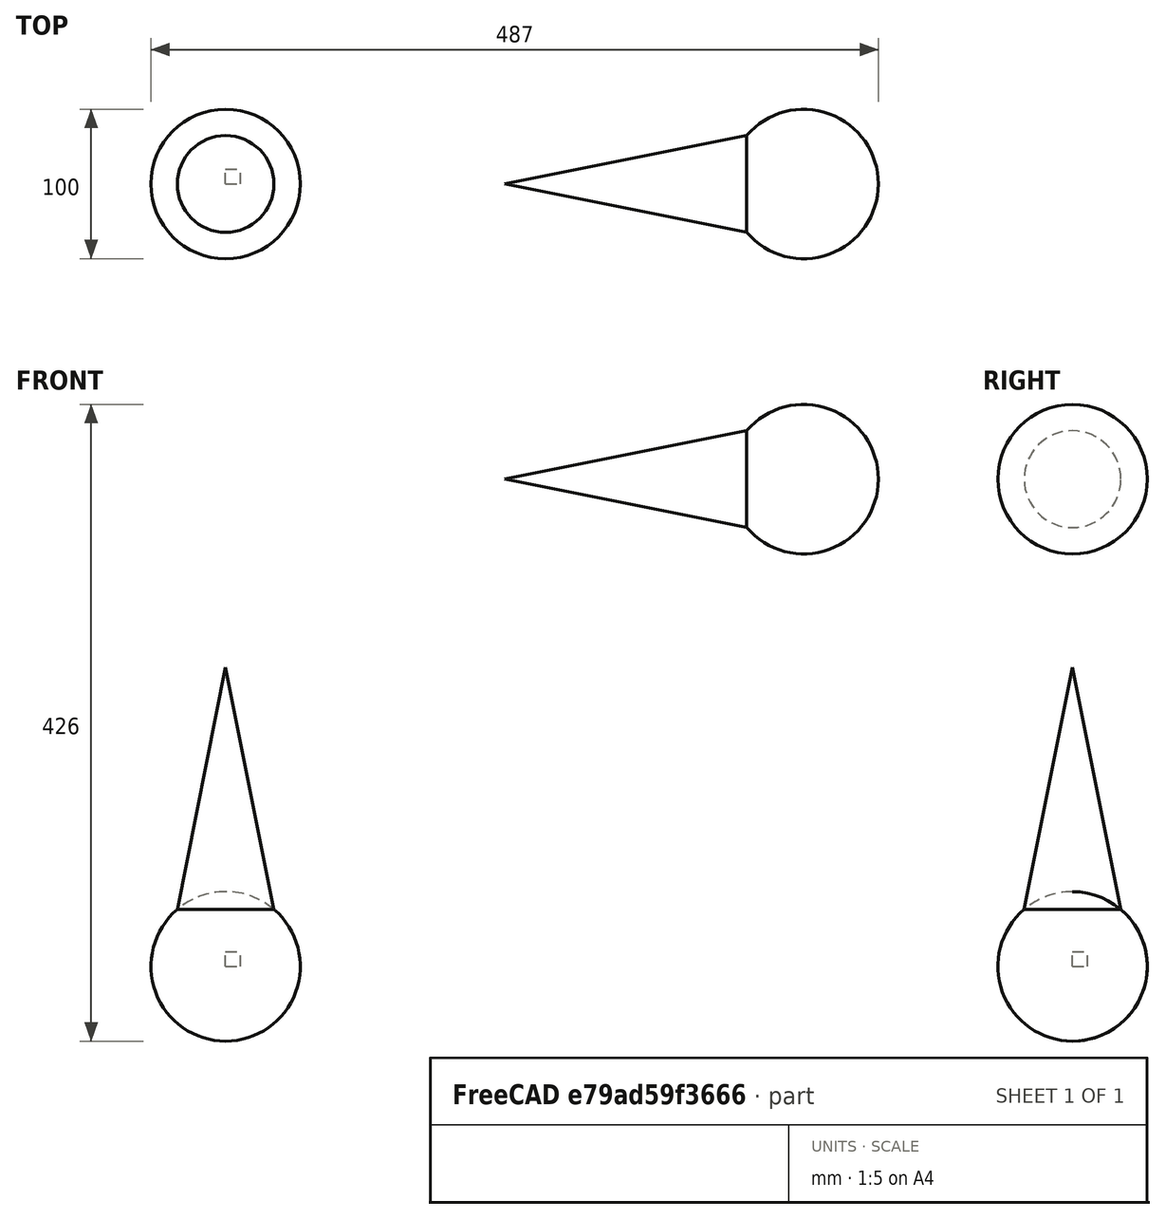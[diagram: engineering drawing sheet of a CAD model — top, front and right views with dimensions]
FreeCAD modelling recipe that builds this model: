
FCSTD DOCUMENT  (FreeCAD 0.22R36526 (Git))
Label: Bungee
License: All rights reserved
LicenseURL: http://en.wikipedia.org/wiki/All_rights_reserved
objects: App::DocumentObjectGroupPython×59, PartDesign::CoordinateSystem×7, App::Part×3, App::TextDocument×3, Part::Line×3, App::FeaturePython×3, Part::Sphere×2, Part::FeaturePython×2, App::MaterialObjectPython×2, Part::Cone×1, Part::MultiFuse×1, Part::Box×1
note: 17 computed .brp shape members not serialized (recipe doc carries the construction recipe); baked Part::Feature solids carry a one-line shape summary decoded from their .brp

FEATURE [Part::Sphere] Sphere
  Angle1 = -90
  Angle2 = 90
  Angle3 = 360
  AttacherType = Attacher::AttachEngine3D
  Radius = 50
FEATURE [Part::Sphere] Sphere001
  Angle1 = -90
  Angle2 = 90
  Angle3 = 360
  AttacherType = Attacher::AttachEngine3D
  Radius = 50
FEATURE [App::Part] Part  label="Fixed body"
  Group = -> [Sphere]
  Origin = -> Origin
FEATURE [Part::Cone] Cone
  Angle = 360
  AttacherType = Attacher::AttachEngine3D
  Height = 200
  Radius1 = 40
  Radius2 = 0
FEATURE [Part::MultiFuse] Fusion
  Shapes = -> [Sphere001,Cone]
FEATURE [App::Part] Part001  label="Moving body"
  Group = -> [Cone,Sphere001,Fusion]
  Origin = -> Origin001
  Placement = pos=(387,-6e-16,326) rot=(0,-1,0;1.5708rad)
FEATURE [App::DocumentObjectGroupPython] MBD_animated_vectors  # scripted group (container) (typed FeaturePython)
FEATURE [App::DocumentObjectGroupPython] MBD_drives_and_drive_callers  # scripted group (container) (typed FeaturePython)
FEATURE [App::DocumentObjectGroupPython] MBD_abstract_nodes  # scripted group (container) (typed FeaturePython)
FEATURE [App::DocumentObjectGroupPython] MBD_structural_dummy_nodes  # scripted group (container) (typed FeaturePython)
FEATURE [App::DocumentObjectGroupPython] MBD_hydraulic_nodes  # scripted group (container) (typed FeaturePython)
FEATURE [App::DocumentObjectGroupPython] MBD_structural_static_nodes  # scripted group (container) (typed FeaturePython)
FEATURE [App::DocumentObjectGroupPython] MBD_beam_elements  # scripted group (container) (typed FeaturePython)
FEATURE [App::DocumentObjectGroupPython] MBD_genel_clamps  # scripted group (container) (typed FeaturePython)
FEATURE [App::DocumentObjectGroupPython] MBD_genel_elements  # scripted group (container) (typed FeaturePython)
  Group = -> [MBD_genel_clamps]
FEATURE [App::DocumentObjectGroupPython] MBD_hydraulic_fluid_elements  # scripted group (container) (typed FeaturePython)
FEATURE [App::DocumentObjectGroupPython] MBD_hydraulic_elements  # scripted group (container) (typed FeaturePython)
  Group = -> [MBD_hydraulic_fluid_elements]
FEATURE [App::DocumentObjectGroupPython] MBD_angular_acceleration_joints  # scripted group (container) (typed FeaturePython)
FEATURE [App::DocumentObjectGroupPython] MBD_angular_velocity_joints  # scripted group (container) (typed FeaturePython)
FEATURE [App::DocumentObjectGroupPython] MBD_assembly_joints  # scripted group (container) (typed FeaturePython)
FEATURE [App::DocumentObjectGroupPython] MBD_coincidence_joints  # scripted group (container) (typed FeaturePython)
FEATURE [App::DocumentObjectGroupPython] MBD_cylindrical_joints  # scripted group (container) (typed FeaturePython)
FEATURE [App::DocumentObjectGroupPython] MBD_deformable_axial_joints  # scripted group (container) (typed FeaturePython)
FEATURE [App::DocumentObjectGroupPython] MBD_deformable_displacement_joints  # scripted group (container) (typed FeaturePython)
FEATURE [App::DocumentObjectGroupPython] MBD_deformable_hinge_joints  # scripted group (container) (typed FeaturePython)
FEATURE [App::DocumentObjectGroupPython] MBD_distance_joints  # scripted group (container) (typed FeaturePython)
FEATURE [App::DocumentObjectGroupPython] MBD_drive_hinge_joints  # scripted group (container) (typed FeaturePython)
FEATURE [App::DocumentObjectGroupPython] MBD_in_line_joints  # scripted group (container) (typed FeaturePython)
FEATURE [App::DocumentObjectGroupPython] MBD_in_plane_joints  # scripted group (container) (typed FeaturePython)
FEATURE [App::DocumentObjectGroupPython] MBD_linear_acceleration_joints  # scripted group (container) (typed FeaturePython)
FEATURE [App::DocumentObjectGroupPython] MBD_linear_velocity_joints  # scripted group (container) (typed FeaturePython)
FEATURE [App::DocumentObjectGroupPython] MBD_prismatic_joints  # scripted group (container) (typed FeaturePython)
FEATURE [App::DocumentObjectGroupPython] MBD_hinge_joints  # scripted group (container) (typed FeaturePython)
FEATURE [App::DocumentObjectGroupPython] MBD_revolute_pin_joints  # scripted group (container) (typed FeaturePython)
FEATURE [App::DocumentObjectGroupPython] MBD_revolute_rotation_joints  # scripted group (container) (typed FeaturePython)
FEATURE [App::DocumentObjectGroupPython] MBD_shock_absorber_joints  # scripted group (container) (typed FeaturePython)
FEATURE [App::DocumentObjectGroupPython] MBD_slider_joints  # scripted group (container) (typed FeaturePython)
FEATURE [App::DocumentObjectGroupPython] MBD_spherical_hinge_joints  # scripted group (container) (typed FeaturePython)
FEATURE [App::DocumentObjectGroupPython] MBD_total_joints  # scripted group (container) (typed FeaturePython)
FEATURE [App::DocumentObjectGroupPython] MBD_total_pin_joints  # scripted group (container) (typed FeaturePython)
FEATURE [App::DocumentObjectGroupPython] MBD_viscous_body_joints  # scripted group (container) (typed FeaturePython)
FEATURE [App::DocumentObjectGroupPython] MBD_dummy_body_elements  # scripted group (container) (typed FeaturePython)
FEATURE [App::DocumentObjectGroupPython] MBD_gear_body_elements  # scripted group (container) (typed FeaturePython)
FEATURE [App::DocumentObjectGroupPython] MBD_static_body_elements  # scripted group (container) (typed FeaturePython)
FEATURE [App::DocumentObjectGroupPython] MBD_structural_couple_elements  # scripted group (container) (typed FeaturePython)
FEATURE [App::DocumentObjectGroupPython] MBD_structural_force_elements  # scripted group (container) (typed FeaturePython)
FEATURE [App::DocumentObjectGroupPython] MBD_structural_internal_force_elements  # scripted group (container) (typed FeaturePython)
FEATURE [App::DocumentObjectGroupPython] MBD_force_couple_elements  # scripted group (container) (typed FeaturePython)
  Group = -> [MBD_structural_couple_elements,MBD_structural_force_elements,MBD_structural_internal_force_elements]
FEATURE [App::DocumentObjectGroupPython] MBD_scalar_functions  # scripted group (container) (typed FeaturePython)
FEATURE [App::TextDocument] ELEMENT_input_file
  Text = <blob: 10275 chars omitted>
FEATURE [App::TextDocument] ELEMENT_input_file_aux
FEATURE [App::DocumentObjectGroupPython] MBD_input_files  # scripted group (container) (typed FeaturePython)
  Group = -> [ELEMENT_input_file,ELEMENT_input_file_aux]
FEATURE [App::TextDocument] ELEMENT_variables
FEATURE [App::DocumentObjectGroupPython] MBD_user_defined_variables  # scripted group (container) (typed FeaturePython)
  Group = -> [ELEMENT_variables]
FEATURE [Part::Line] ELEMENT_cmx
  AttacherType = Attacher::AttachEngine3D
  X1 = 187
  X2 = -1.6e-15
  Y1 = -6e-16
  Y2 = -6e-16
  Z1 = 326
  Z2 = -1.5e-15
FEATURE [Part::Line] ELEMENT_cmy
  AttacherType = Attacher::AttachEngine3D
  X1 = 0
  X2 = 0
  Y1 = 0
  Y2 = 0
  Z1 = 0
  Z2 = 1
FEATURE [Part::Line] ELEMENT_cmz
  AttacherType = Attacher::AttachEngine3D
  X1 = 0
  X2 = 0
  Y1 = 0
  Y2 = 0
  Z1 = 0
  Z2 = 1
FEATURE [Part::Box] bbox
  AttacherType = Attacher::AttachEngine3D
  Height = 10
  Length = 10
  Width = 10
FEATURE [PartDesign::CoordinateSystem] ELEMENT_ground
  AttacherType = Attacher::AttachEngine3D
FEATURE [App::DocumentObjectGroupPython] MBD_global_reference_frame  # scripted group (container) (typed FeaturePython)
  Group = -> [ELEMENT_cmx,ELEMENT_cmy,ELEMENT_cmz,ELEMENT_ground,bbox]
FEATURE [App::FeaturePython] ELEMENT_parameters  # WARN: FeaturePython — macro-defined, semantics opaque (R4)
  assembly_max_iterations = 1000
  default_orientation = 0
  derivatives_coefficient = auto
  derivatives_max_iterations = 100
  derivatives_tolerance = 0.0001
  final_time = 4
  initial_position_stiffness = 1
  initial_time = 0
  initial_velocity_stiffness = 1
  integration_max_iterations = 100
  model = 0
  modules_to_load = 0
  omega_rotates = 0
  output_data = 0
  output_meter = 1
  path_to_ELEMENT_executable = <userpath>/.local/share/FreeCAD/Mod/FreeCAD-motion-workbench-master/mbdyn-1.7.3-executables/LinuxExecutable/mbdyn
  print = 0
  skip_initial_joint_assembly = 0
  solver = 0
  time_step = 0.01
  tolerance = 1e-06
  type_of_path_to_ELEMENT_executable = 0
  type_of_path_to_run_time_loadable_modules = 0
  type_of_working_directory = 0
  units = 0
FEATURE [App::FeaturePython] ELEMENT_animation  # WARN: FeaturePython — macro-defined, semantics opaque (R4)
  animationClicked = false
  assembled = false
  association0 = none
  association1 = none
  association2 = none
  association3 = none
  association4 = none
  association5 = none
  association6 = none
  association7 = none
  association8 = none
  association9 = none
  bodies_line_width = 1
  bodies_point_size = 4
  characteristic_length = 1.5e+100
  continous = true
  current_time = 0
  current_time_step = 0
  follow_selected_object = false
  highlight_element = true
  objects_to_animate = 0
  speed = 10
  stop_at_time = 0
  stop_at_time_step = 0
  subAssembly = true
  transparency_when_exploded = 50
  zoon_when_contracted = 0.5
  zoon_when_expanded = 1
FEATURE [App::DocumentObjectGroupPython] MBD_simulation_parameters  # scripted group (container) (typed FeaturePython)
  Group = -> [ELEMENT_parameters,ELEMENT_animation]
FEATURE [Part::FeaturePython] ELEMENT_rigid_body_1  # WARN: FeaturePython — macro-defined, semantics opaque (R4)
  absolute_center_of_mass_X = -8e-16
  absolute_center_of_mass_Y = -1.4e-15
  absolute_center_of_mass_Z = 4e-16
  assembly_stage = 1
  base_entity = Part
  densities = [7900]
  first_axes_of_inertia_x = [0.932625]
  first_axes_of_inertia_y = [0.360846]
  first_axes_of_inertia_z = [1.11022e-16]
  fixed = false
  label = 1
  masses = [4.13643]
  material_definitions = [0]
  materials = steel
  node = 1
  principal_moments_of_inertia_x = [0.00413643]
  principal_moments_of_inertia_y = [0.00413643]
  principal_moments_of_inertia_z = [0.00413643]
  relative_centers_of_mass_x = [0]
  relative_centers_of_mass_y = [0]
  relative_centers_of_mass_z = [0]
  second_axes_of_inertia_x = [1.11022e-16]
  second_axes_of_inertia_y = [0]
  second_axes_of_inertia_z = [-1]
  third_axes_of_inertia_x = [-0.360846]
  third_axes_of_inertia_y = [0.932625]
  third_axes_of_inertia_z = [-9.6969e-19]
  total_mass = 4.13643
  transparency_when_assembled = 0
  type = rigid
  volumes = [0.000523599]
FEATURE [App::MaterialObjectPython] ELEMENT_material_1  # material (typed FeaturePython)
  Category = 0
  Material = Density=7900.00 kg/m^3; Name=Steel-Generic
FEATURE [PartDesign::CoordinateSystem] ELEMENT_structural_dynamic_1
  AttacherType = Attacher::AttachEngine3D
  Placement = pos=(-8e-16,-1.4e-15,4e-16) rot=(0,0,1;0rad)
  absolute_angular_velocity_X = 0
  absolute_angular_velocity_Y = 0
  absolute_angular_velocity_Z = 0
  absolute_orientation_matrix = 3, 0.0, 0.0, 1.0, 2, 0.0, 1.0, 0.0
  absolute_position_X = -8e-16
  absolute_position_Y = -1.4e-15
  absolute_position_Z = 4e-16
  absolute_velocity_X = 0
  absolute_velocity_Y = 0
  absolute_velocity_Z = 0
  base_entity = -> ELEMENT_rigid_body_1
  initial_conditions_reference_system_angular_velocity = 0
  initial_conditions_reference_system_velocity = 0
  label = 1
  offset_pitch = 0
  offset_reference_system_orientation = 0
  offset_reference_system_position = 0
  offset_roll = 0
  offset_x = 0
  offset_y = 0
  offset_yaw = 0
  offset_z = 0
  placement_method = 0
  plugin_variables = none
  type = dynamic
FEATURE [PartDesign::CoordinateSystem] ELEMENT_clamp_joint_1
  AttacherType = Attacher::AttachEngine3D
  Placement = pos=(-8e-16,-1.4e-15,4e-16) rot=(0,0,1;0rad)
  absolute_orientation_matrix = 3, 0.0, 0.0, 1.0, 2, 0.0, 1.0, 0.0
  absolute_pin_position_X = -8e-16
  absolute_pin_position_Y = -1.4e-15
  absolute_pin_position_Z = 4e-16
  assembly_joint = false
  base_entity = -> ELEMENT_rigid_body_1
  driven_element = false
  driven_element_expression = Time <= 1.0
  group = 0
  joint = clamp
  joint_activation = 0
  label = 1
  plugin_variables = none
FEATURE [App::DocumentObjectGroupPython] MBD_clamp_joints  # scripted group (container) (typed FeaturePython)
  Group = -> [ELEMENT_clamp_joint_1]
FEATURE [Part::FeaturePython] ELEMENT_rigid_body_2  # WARN: FeaturePython — macro-defined, semantics opaque (R4)
  Placement = pos=(387,-6e-16,326) rot=(0,-1,0;1.5708rad)
  absolute_center_of_mass_X = 367.754
  absolute_center_of_mass_Y = 1.4e-15
  absolute_center_of_mass_Z = 326
  assembly_stage = 1
  base_entity = Part001
  densities = [7900]
  first_axes_of_inertia_x = [-9.15432e-16]
  first_axes_of_inertia_y = [0.0181987]
  first_axes_of_inertia_z = [0.999834]
  fixed = false
  label = 2
  masses = [5.37893]
  material_definitions = [0]
  materials = steel
  node = 2
  principal_moments_of_inertia_x = [0.0120977]
  principal_moments_of_inertia_y = [0.0120977]
  principal_moments_of_inertia_z = [0.00452028]
  relative_centers_of_mass_x = [0]
  relative_centers_of_mass_y = [0]
  relative_centers_of_mass_z = [0]
  second_axes_of_inertia_x = [2.42614e-17]
  second_axes_of_inertia_y = [0.999834]
  second_axes_of_inertia_z = [-0.0181987]
  third_axes_of_inertia_x = [1]
  third_axes_of_inertia_y = [-7.59775e-18]
  third_axes_of_inertia_z = [9.15722e-16]
  total_mass = 5.37893
  transparency_when_assembled = 0
  type = rigid
  volumes = [0.000680877]
FEATURE [App::DocumentObjectGroupPython] MBD_rigid_body_elements  # scripted group (container) (typed FeaturePython)
  Group = -> [ELEMENT_rigid_body_1,ELEMENT_rigid_body_2]
FEATURE [App::Part] MBD_body_elements
  Group = -> [MBD_dummy_body_elements,MBD_rigid_body_elements,MBD_gear_body_elements,MBD_static_body_elements,ELEMENT_rigid_body_1,ELEMENT_rigid_body_2]
  Origin = -> Origin002
FEATURE [App::MaterialObjectPython] ELEMENT_material_2  # material (typed FeaturePython)
  Category = 0
  Material = Density=7900.00 kg/m^3; Name=Steel-Generic
FEATURE [App::DocumentObjectGroupPython] MBD_materials  # scripted group (container) (typed FeaturePython)
  Group = -> [ELEMENT_material_1,ELEMENT_material_2]
FEATURE [PartDesign::CoordinateSystem] ELEMENT_structural_dynamic_2
  AttacherType = Attacher::AttachEngine3D
  Placement = pos=(367.754,1.4e-15,326) rot=(0,-1,0;1.5708rad)
  absolute_angular_velocity_X = 0
  absolute_angular_velocity_Y = 0
  absolute_angular_velocity_Z = 0
  absolute_orientation_matrix = 3, -1.0, -0.0, 2.220446049250313e-16, 2, -0.0, 1.0, 0.0
  absolute_position_X = 367.754
  absolute_position_Y = 1.4e-15
  absolute_position_Z = 326
  absolute_velocity_X = 0
  absolute_velocity_Y = 0
  absolute_velocity_Z = 0
  base_entity = -> ELEMENT_rigid_body_2
  initial_conditions_reference_system_angular_velocity = 0
  initial_conditions_reference_system_velocity = 0
  label = 2
  offset_pitch = 0
  offset_reference_system_orientation = 0
  offset_reference_system_position = 0
  offset_roll = 0
  offset_x = 0
  offset_y = 0
  offset_yaw = 0
  offset_z = 0
  placement_method = 0
  plugin_variables = none
  type = dynamic
FEATURE [App::DocumentObjectGroupPython] MBD_structural_dynamic_nodes  # scripted group (container) (typed FeaturePython)
  Group = -> [ELEMENT_structural_dynamic_1,ELEMENT_structural_dynamic_2]
FEATURE [App::DocumentObjectGroupPython] MBD_nodes  # scripted group (container) (typed FeaturePython)
  Group = -> [MBD_abstract_nodes,MBD_structural_dummy_nodes,MBD_structural_dynamic_nodes,MBD_hydraulic_nodes,MBD_structural_static_nodes]
FEATURE [App::FeaturePython] ELEMENT_constitutive_law_1  # WARN: FeaturePython — macro-defined, semantics opaque (R4)
  _3Dsa11 = 1
  _3Dsa12 = 0
  _3Dsa13 = 0
  _3Dsa21 = 0
  _3Dsa22 = 1
  _3Dsa23 = 0
  _3Dsa31 = 0
  _3Dsa32 = 0
  _3Dsa33 = 1
  _3Dva11 = 0.001
  _3Dva12 = 0
  _3Dva13 = 0
  _3Dva21 = 0
  _3Dva22 = 0.001
  _3Dva23 = 0
  _3Dva31 = 0
  _3Dva32 = 0
  _3Dva33 = 0.001
  _6Dsa11 = 1
  _6Dsa12 = 0
  _6Dsa13 = 0
  _6Dsa14 = 0
  _6Dsa15 = 0
  _6Dsa16 = 0
  _6Dsa21 = 0
  _6Dsa22 = 1
  _6Dsa23 = 0
  _6Dsa24 = 0
  _6Dsa25 = 0
  _6Dsa26 = 0
  _6Dsa31 = 0
  _6Dsa32 = 0
  _6Dsa33 = 1
  _6Dsa34 = 0
  _6Dsa35 = 0
  _6Dsa36 = 0
  _6Dsa41 = 0
  _6Dsa42 = 0
  _6Dsa43 = 0
  _6Dsa44 = 1
  _6Dsa45 = 0
  _6Dsa46 = 0
  _6Dsa51 = 0
  _6Dsa52 = 0
  _6Dsa53 = 0
  _6Dsa54 = 0
  _6Dsa55 = 1
  _6Dsa56 = 0
  _6Dsa61 = 0
  _6Dsa62 = 0
  _6Dsa63 = 0
  _6Dsa64 = 0
  _6Dsa65 = 0
  _6Dsa66 = 1
  _6Dva11 = 0.001
  _6Dva12 = 0
  _6Dva13 = 0
  _6Dva14 = 0
  _6Dva15 = 0
  _6Dva16 = 0
  _6Dva21 = 0
  _6Dva22 = 0.001
  _6Dva23 = 0
  _6Dva24 = 0
  _6Dva25 = 0
  _6Dva26 = 0
  _6Dva31 = 0
  _6Dva32 = 0
  _6Dva33 = 0.001
  _6Dva34 = 0
  _6Dva35 = 0
  _6Dva36 = 0
  _6Dva41 = 0
  _6Dva42 = 0
  _6Dva43 = 0
  _6Dva44 = 0.001
  _6Dva45 = 0
  _6Dva46 = 0
  _6Dva51 = 0
  _6Dva52 = 0
  _6Dva53 = 0
  _6Dva54 = 0
  _6Dva55 = 0.001
  _6Dva56 = 0
  _6Dva61 = 0
  _6Dva62 = 0
  _6Dva63 = 0
  _6Dva64 = 0
  _6Dva65 = 0
  _6Dva66 = 0.001
  dimensionality = 0
  expression = linear elastic isotropic, 100.0
  label = 1
  stiffness = 100
  type = 0
  viscosity = 0.001
FEATURE [App::DocumentObjectGroupPython] MBD_constitutive_laws  # scripted group (container) (typed FeaturePython)
  Group = -> [ELEMENT_constitutive_law_1]
FEATURE [PartDesign::CoordinateSystem] ELEMENT_marker_2_1
  AttacherType = Attacher::AttachEngine3D
  Placement = pos=(187,-6e-16,326) rot=(0,0,1;0rad)
  base_entity = -> ELEMENT_rigid_body_2
  label = 2
  offset_pitch = 0
  offset_reference_system_orientation = 0
  offset_reference_system_position = 0
  offset_roll = 0
  offset_x = 0
  offset_y = 0
  offset_yaw = 0
  offset_z = 0
  placement_method = 1
  position_reference_1 = -> ELEMENT_rigid_body_2 [Vertex3]
FEATURE [App::DocumentObjectGroupPython] MBD_markers  # scripted group (container) (typed FeaturePython)
  Group = -> [ELEMENT_marker_2_1]
FEATURE [PartDesign::CoordinateSystem] ELEMENT_rod_joint_2
  AttacherType = Attacher::AttachEngine3D
  Placement = pos=(-1.6e-15,-6e-16,-1.5e-15) rot=(0,0,1;0rad)
  action_entity = -> ELEMENT_marker_2_1
  assembly_joint = false
  base_entity = -> ELEMENT_rigid_body_1
  constitutive_law = -> ELEMENT_constitutive_law_1
  driven_element = false
  driven_element_expression = Time <= 1.0
  joint = rod
  joint_activation = 0
  label = 2
  offset_pitch = 0
  offset_reference_system_orientation = 0
  offset_reference_system_position = 0
  offset_roll = 0
  offset_x = 0
  offset_y = 0
  offset_yaw = 0
  offset_z = 0
  placement_method = 1
  plugin_variables = none
  position_reference_1 = -> ELEMENT_rigid_body_1 [Face1]
  relative_arm_1 = -7.779880773641398e-19, 7.873338210045535e-19, -1.8917489796876907e-18
  relative_arm_2 = 5.684341886080802e-17, -1.995615177952912e-18, 0.1807541176523111
  rod_length = 375.826
FEATURE [App::DocumentObjectGroupPython] MBD_rod_joints  # scripted group (container) (typed FeaturePython)
  Group = -> [ELEMENT_rod_joint_2]
FEATURE [App::DocumentObjectGroupPython] MBD_joint_elements  # scripted group (container) (typed FeaturePython)
  Group = -> [MBD_angular_acceleration_joints,MBD_angular_velocity_joints,MBD_assembly_joints,MBD_clamp_joints,MBD_coincidence_joints,MBD_cylindrical_joints,MBD_deformable_axial_joints,MBD_deformable_displacement_joints,MBD_deformable_hinge_joints,MBD_distance_joints,MBD_drive_hinge_joints,MBD_in_line_joints,MBD_in_plane_joints,MBD_linear_acceleration_joints,MBD_linear_velocity_joints,MBD_prismatic_joints,+10 more]
FEATURE [PartDesign::CoordinateSystem] ELEMENT_gravity_1
  AttacherType = Attacher::AttachEngine3D
  direction = 0.0, 0.0, 1.0
  driven_element = false
  driven_element_expression = Time < 4.
  gravity_acceleration = 9.807
  label = 1
  offset_pitch = 0
  offset_reference_system_orientation = 0
  offset_reference_system_position = 0
  offset_roll = 0
  offset_x = 0
  offset_y = 0
  offset_yaw = 0
  offset_z = 0
  placement_method = 1
  type = uniform
FEATURE [App::DocumentObjectGroupPython] MBD_gravity_elements  # scripted group (container) (typed FeaturePython)
  Group = -> [ELEMENT_gravity_1]
FEATURE [App::DocumentObjectGroupPython] MBD_elements  # scripted group (container) (typed FeaturePython)
  Group = -> [MBD_beam_elements,MBD_body_elements,MBD_genel_elements,MBD_gravity_elements,MBD_hydraulic_elements,MBD_joint_elements,MBD_force_couple_elements]
FEATURE [App::DocumentObjectGroupPython] MBD_simulation  # scripted group (container) (typed FeaturePython)
  Group = -> [MBD_animated_vectors,MBD_constitutive_laws,MBD_drives_and_drive_callers,MBD_global_reference_frame,MBD_input_files,MBD_materials,MBD_markers,MBD_nodes,MBD_elements,MBD_simulation_parameters,MBD_scalar_functions,MBD_user_defined_variables]
